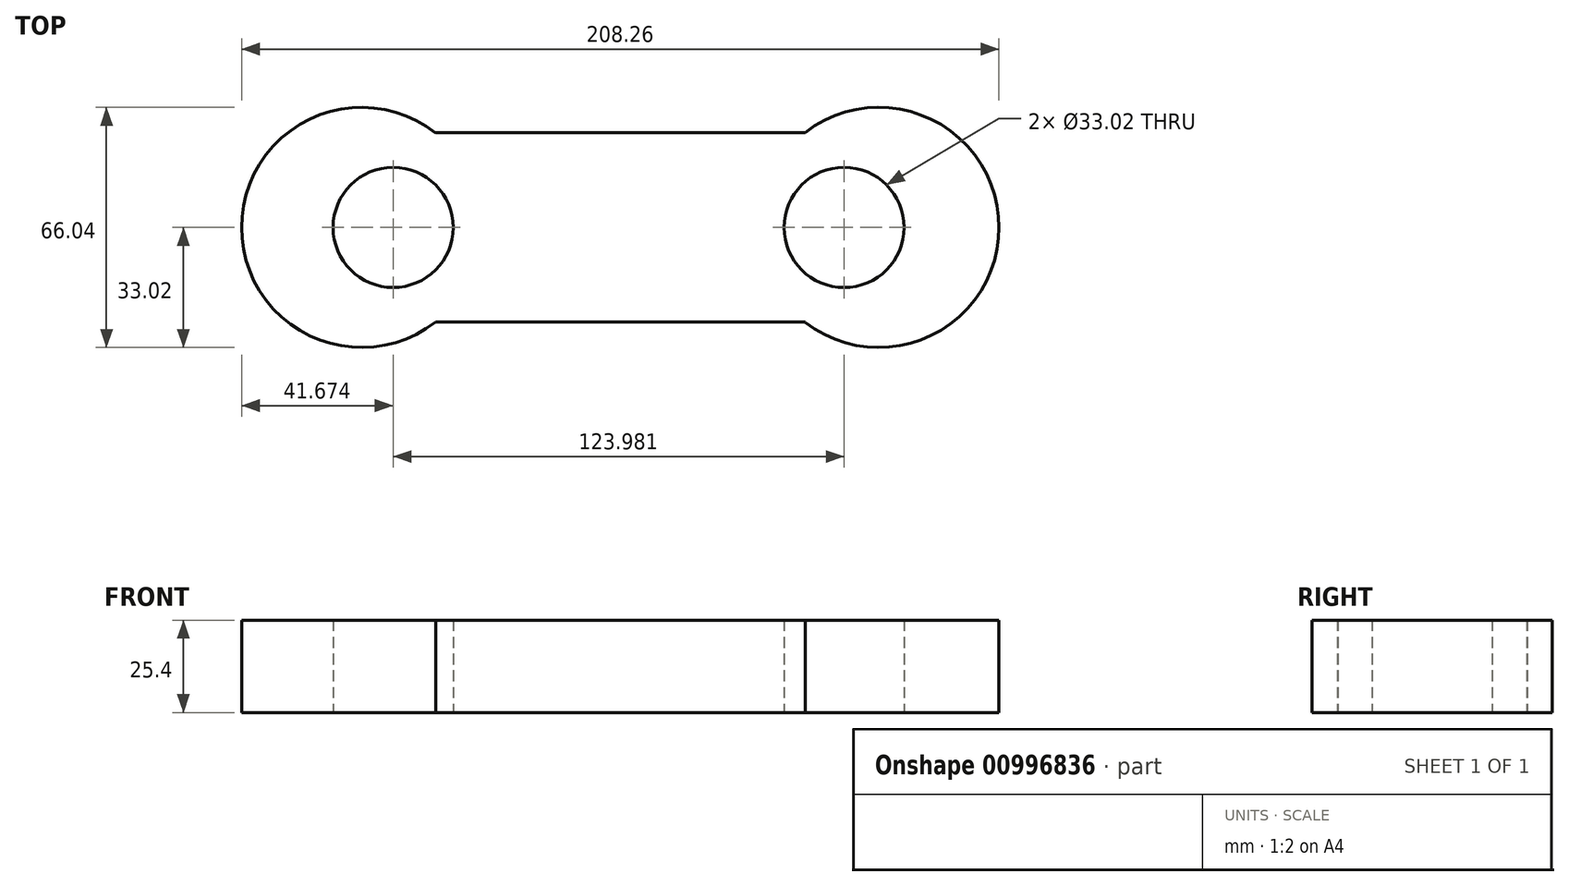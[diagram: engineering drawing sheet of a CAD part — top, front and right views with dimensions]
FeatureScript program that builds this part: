
annotation { "Feature Type Name" : "Feature", "Feature Type Description" : "" }
export const myFeature = defineFeature(function(context is Context, id is Id, definition is map)
    precondition{}
    {
        {
            var Q0;
            Q0=qCreatedBy(makeId("Top.planeOp"),FACE);
            var sketch = newSketch(context, id + "F0", { "sketchPlane" : qUnion([Q0])});
            skLineSegment(sketch, "E0.bottom", {"start": v(38.2, 26.02) * mm, "end": v(-63.4, 26.02) * mm});
            skLineSegment(sketch, "E0.top", {"start": v(38.2, -26.02) * mm, "end": v(-63.4, -26.02) * mm});
            skLineSegment(sketch, "E0.left", {"start": v(38.2, 26.09) * mm, "end": v(38.2, 26.02) * mm});
            skLineSegment(sketch, "E0.right", {"start": v(-63.4, 26.02) * mm, "end": v(-63.4, 25.99) * mm});
            skPoint(sketch, "E0.middle", {"position": v(-12.6, 0) * mm});
            skArc(sketch, "E1", {"start": v(38.2, -26.09) * mm, "mid": v(91.46, 0) * mm, "end": v(38.2, 26.09) * mm});
            skLineSegment(sketch, "E2.trimOffspring", {"start": v(38.2, -26.02) * mm, "end": v(38.2, -26.09) * mm});
            skArc(sketch, "E3", {"start": v(-63.4, 25.99) * mm, "mid": v(-116.8, 0) * mm, "end": v(-63.4, -25.99) * mm});
            skLineSegment(sketch, "E4.trimOffspring", {"start": v(-63.4, -25.99) * mm, "end": v(-63.4, -26.02) * mm});
            skCircle(sketch, "E5", {"center": v(-75.13, 0) * mm, "radius": 16.51 * mm});
            skCircle(sketch, "E6", {"center": v(48.86, 0) * mm, "radius": 16.51 * mm});
            skSolve(sketch);
        }
        {
            var Q0;
            Q0=makeQuery(id+"F0.imprint","IMPRINT",FACE,{"disambiguationData":[TD([[makeQuery(id+"F0.imprint","IMPRINT",EDGE,{"derivedFrom":sQuery(id+"F0.wireOp",EDGE,"E0.bottom")}),1.0]])]});
            var sketch = newSketch(context, id + "F1", { "sketchPlane" : qUnion([Q0])});
            skSolve(sketch);
        }
        {
            var Q0;
            Q0 = qSketchRegion(id + "F1", true);
            var Q1;
            Q1=makeQuery(id+"F0.imprint","IMPRINT",FACE,{"disambiguationData":[TD([[makeQuery(id+"F0.imprint","IMPRINT",EDGE,{"derivedFrom":sQuery(id+"F0.wireOp",EDGE,"E0.bottom")}),1.0]])]});
            extrude(context, id + "F2", {"entities" : qUnion([Q0, Q1]), "depth" : 25.4 * mm, "offsetDistance" : 25.4 * mm});
        }
    });
